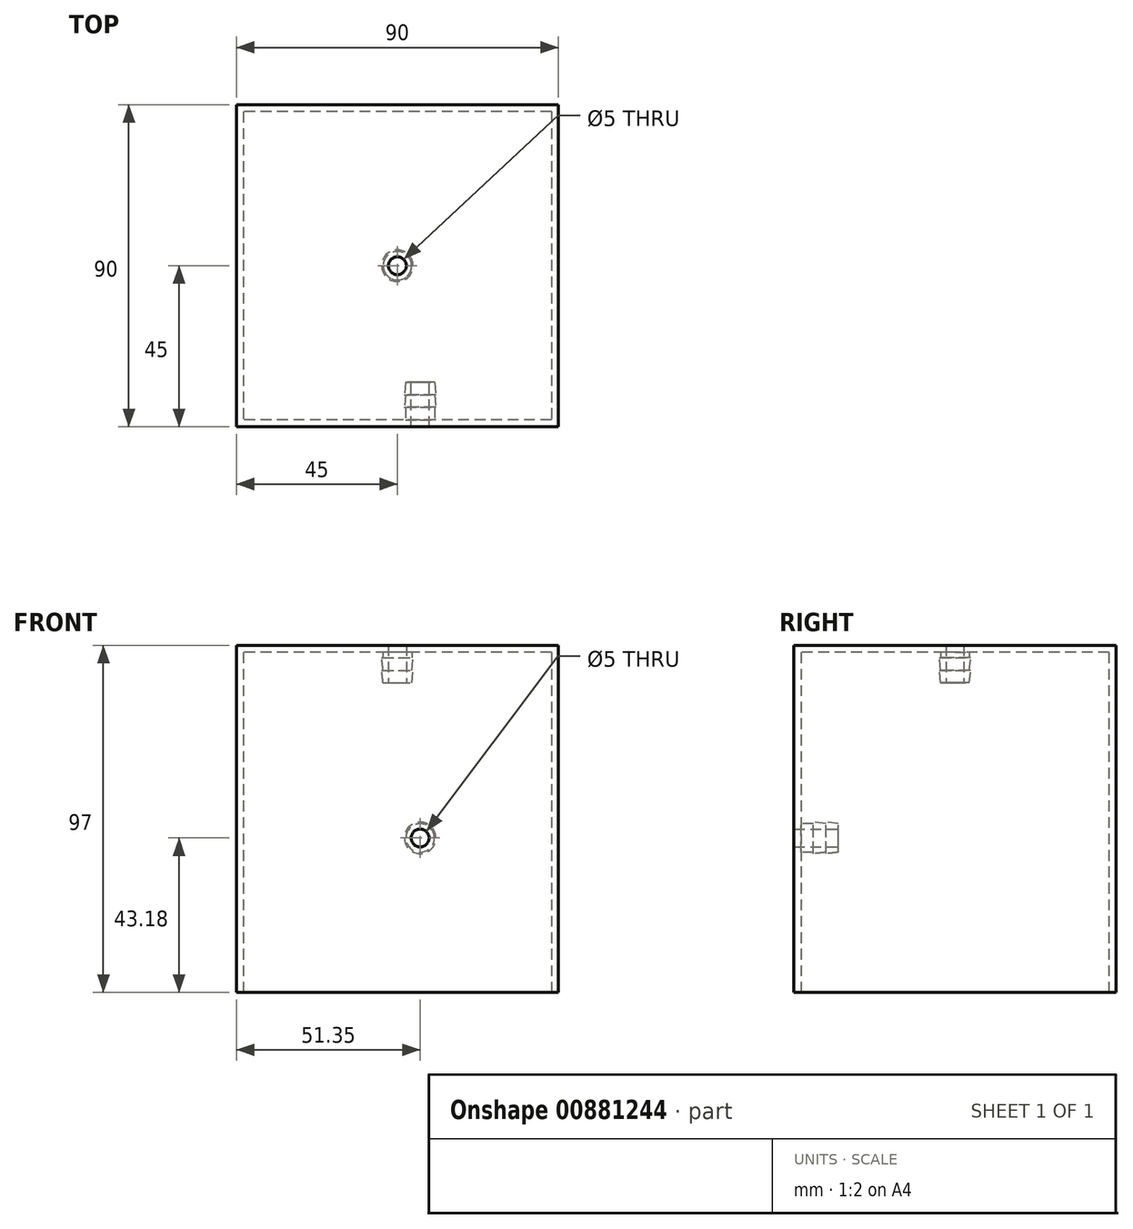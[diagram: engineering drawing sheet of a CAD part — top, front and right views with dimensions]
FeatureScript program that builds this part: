
annotation { "Feature Type Name" : "Feature", "Feature Type Description" : "" }
export const myFeature = defineFeature(function(context is Context, id is Id, definition is map)
    precondition{}
    {
        {
            var Q0;
            Q0=qCreatedBy(makeId("Top.planeOp"),FACE);
            var sketch = newSketch(context, id + "F0", { "sketchPlane" : qUnion([Q0])});
            skLineSegment(sketch, "E0.bottom", {"start": v(45, 45) * mm, "end": v(-45, 45) * mm});
            skLineSegment(sketch, "E0.top", {"start": v(45, -45) * mm, "end": v(-45, -45) * mm});
            skLineSegment(sketch, "E0.left", {"start": v(45, 45) * mm, "end": v(45, -45) * mm});
            skLineSegment(sketch, "E0.right", {"start": v(-45, 45) * mm, "end": v(-45, -45) * mm});
            skPoint(sketch, "E0.middle", {"position": v(0, 0) * mm});
            skLineSegment(sketch, "E1.0", {"start": v(43, 43) * mm, "end": v(-43, 43) * mm});
            skLineSegment(sketch, "E1.1", {"start": v(43, 43) * mm, "end": v(43, -43) * mm});
            skLineSegment(sketch, "E1.2", {"start": v(43, -43) * mm, "end": v(-43, -43) * mm});
            skLineSegment(sketch, "E1.3", {"start": v(-43, 43) * mm, "end": v(-43, -43) * mm});
            skSolve(sketch);
        }
        {
            var Q0;
            Q0 = qSketchRegion(id + "F0", true);
            extrude(context, id + "F1", {"entities" : qUnion([Q0]), "depth" : 97 * mm, "offsetDistance" : 25 * mm});
        }
        {
            var Q0;
            Q0=makeQuery(id+"F1.opExtrude","CAP_FACE",FACE,{"disambiguationData":[OSD([sQuery(id+"F0.wireOp",EDGE,"E0.bottom"),sQuery(id+"F0.wireOp",EDGE,"E0.top"),sQuery(id+"F0.wireOp",EDGE,"E0.left"),sQuery(id+"F0.wireOp",EDGE,"E0.right"),sQuery(id+"F0.wireOp",EDGE,"E1.0"),sQuery(id+"F0.wireOp",EDGE,"E1.1"),sQuery(id+"F0.wireOp",EDGE,"E1.2"),sQuery(id+"F0.wireOp",EDGE,"E1.3")])],"isStart":false});
            var sketch = newSketch(context, id + "F2", { "sketchPlane" : qUnion([Q0])});
            skLineSegment(sketch, "E2.0", {"start": v(43, 43) * mm, "end": v(43, -43) * mm});
            skLineSegment(sketch, "E2.1", {"start": v(43, 43) * mm, "end": v(-43, 43) * mm});
            skLineSegment(sketch, "E2.2", {"start": v(-43, 43) * mm, "end": v(-43, -43) * mm});
            skLineSegment(sketch, "E2.3", {"start": v(43, -43) * mm, "end": v(-43, -43) * mm});
            skCircle(sketch, "E3", {"center": v(0, 0) * mm, "radius": 4 * mm});
            skSolve(sketch);
        }
        {
            var Q0;
            Q0 = qSketchRegion(id + "F2", true);
            extrude(context, id + "F3", {"entities" : qUnion([Q0]), "operationType" : NewBodyOperationType.ADD, "oppositeDirection" : true, "depth" : 2 * mm, "offsetDistance" : 25 * mm});
        }
        {
            var Q0;
            Q0=qCreatedBy(makeId("Front.planeOp"),FACE);
            var sketch = newSketch(context, id + "F4", { "sketchPlane" : qUnion([Q0])});
            skLineSegment(sketch, "E4", {"start": v(-4, 97) * mm, "end": v(-2.5, 97) * mm});
            skLineSegment(sketch, "E5", {"start": v(-4, 95) * mm, "end": v(-4, 93.5) * mm});
            skLineSegment(sketch, "E6.0", {"start": v(-2.5, 97) * mm, "end": v(-2.5, 86.5) * mm});
            skLineSegment(sketch, "E7", {"start": v(-4, 93.5) * mm, "end": v(-4.4, 93.5) * mm});
            skLineSegment(sketch, "E8", {"start": v(-4.4, 93.5) * mm, "end": v(-4, 90) * mm});
            skLineSegment(sketch, "E9", {"start": v(-4, 90) * mm, "end": v(-4.4, 90) * mm});
            skLineSegment(sketch, "E10", {"start": v(-4.4, 90) * mm, "end": v(-4, 86.5) * mm});
            skLineSegment(sketch, "E11", {"start": v(-4, 86.5) * mm, "end": v(-2.5, 86.5) * mm});
            skLineSegment(sketch, "E12", {"start": v(-4, 95) * mm, "end": v(-4, 97) * mm});
            skSolve(sketch);
        }
        {
            var Q0;
            Q0=qCreatedBy(makeId("Front.planeOp"),FACE);
            var sketch = newSketch(context, id + "F5", { "sketchPlane" : qUnion([Q0])});
            skLineSegment(sketch, "E13", {"start": v(0, 0) * mm, "end": v(0, 103.69) * mm, "construction": true});
            skSolve(sketch);
        }
        {
            var Q0;
            Q0=qSketchRegion(id+"F4",true);
            var Q1;
            Q1=sQuery(id+"F5.wireOp",EDGE,"E13");
            revolve(context, id + "F6", {"operationType" : NewBodyOperationType.ADD, "surfaceOperationType" : NewSurfaceOperationType.NEW, "entities" : qUnion([Q0]), "axis" : qUnion([Q1]), "revolveType" : RevolveType.FULL});
        }
        {
            var Q0;
            Q0=qCreatedBy(makeId("Front.planeOp"),FACE);
            var sketch = newSketch(context, id + "F7", { "sketchPlane" : qUnion([Q0])});
            skCircle(sketch, "E14", {"center": v(6.35, 43.18) * mm, "radius": 2.5 * mm});
            skSolve(sketch);
        }
        {
            var Q0;
            Q0=qSketchRegion(id+"F7",true);
            extrude(context, id + "F8", {"entities" : qUnion([Q0]), "operationType" : NewBodyOperationType.REMOVE, "depth" : 76.2 * mm, "offsetDistance" : 25.4 * mm});
        }
        {
            var Q0;
            Q0=qCreatedBy(makeId("Right.planeOp"),FACE);
            cPlane(context, id + "F9", {"entities" : qUnion([Q0]), "cplaneType" : CPlaneType.OFFSET, "offset" : 6.35 * mm, "width" : 152.4 * mm, "height" : 152.4 * mm});
        }
        {
            var Q0;
            Q0=qCreatedBy(id+"F9.planeOp",FACE);
            var sketch = newSketch(context, id + "F10", { "sketchPlane" : qUnion([Q0])});
            skLineSegment(sketch, "E15", {"start": v(-39.23, 43.18) * mm, "end": v(6.21, 43.18) * mm, "construction": true});
            skSolve(sketch);
        }
        {
            var Q0;
            Q0=qCreatedBy(id+"F9.planeOp",FACE);
            var sketch = newSketch(context, id + "F11", { "sketchPlane" : qUnion([Q0])});
            skLineSegment(sketch, "E16.0", {"start": v(-39.23, 43.18) * mm, "end": v(6.21, 43.18) * mm, "construction": true});
            skLineSegment(sketch, "E17.0", {"start": v(-43.06, 47.18) * mm, "end": v(10.22, 47.18) * mm});
            skLineSegment(sketch, "E18.0", {"start": v(-43.06, 45.68) * mm, "end": v(10.22, 45.68) * mm});
            skLineSegment(sketch, "E19", {"start": v(-43.06, 48.33) * mm, "end": v(-43.06, 44.59) * mm});
            skLineSegment(sketch, "E20.0", {"start": v(-39.56, 47.58) * mm, "end": v(-39.56, 47.18) * mm});
            skLineSegment(sketch, "E21", {"start": v(-39.56, 47.58) * mm, "end": v(-36.06, 47.18) * mm});
            skLineSegment(sketch, "E22", {"start": v(-36.06, 47.18) * mm, "end": v(-36.06, 47.58) * mm});
            skLineSegment(sketch, "E23", {"start": v(-36.06, 47.58) * mm, "end": v(-32.56, 47.18) * mm});
            skLineSegment(sketch, "E24", {"start": v(-32.56, 47.18) * mm, "end": v(-32.56, 45.68) * mm});
            skSolve(sketch);
        }
        {
            var Q0;
            Q0=qSketchRegion(id+"F11",true);
            var Q1;
            Q1=sQuery(id+"F11.wireOp",EDGE,"E16.0");
            revolve(context, id + "F12", {"operationType" : NewBodyOperationType.ADD, "surfaceOperationType" : NewSurfaceOperationType.NEW, "entities" : qUnion([Q0]), "axis" : qUnion([Q1]), "revolveType" : RevolveType.FULL});
        }
    });
